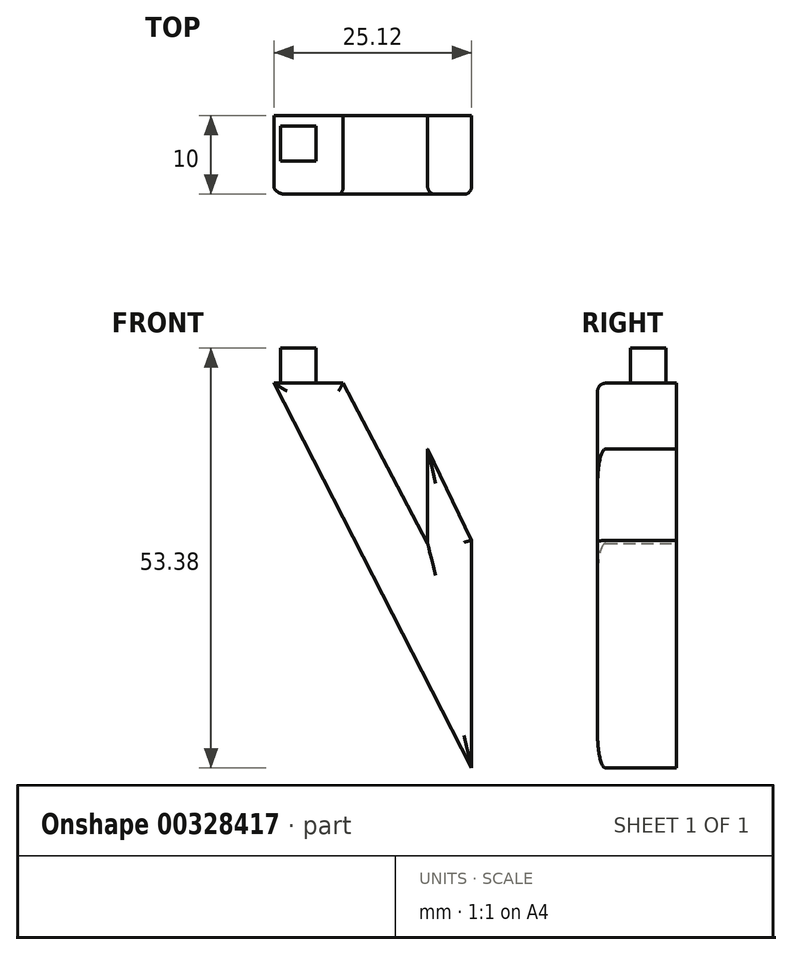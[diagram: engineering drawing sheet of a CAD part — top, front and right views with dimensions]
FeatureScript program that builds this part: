
annotation { "Feature Type Name" : "Feature", "Feature Type Description" : "" }
export const myFeature = defineFeature(function(context is Context, id is Id, definition is map)
    precondition{}
    {
        {
            var Q0;
            Q0=qCreatedBy(makeId("Front.planeOp"),FACE);
            var sketch = newSketch(context, id + "F0", { "sketchPlane" : qUnion([Q0])});
            skLineSegment(sketch, "E0", {"start": v(0, 0) * mm, "end": v(-9, 0) * mm});
            skLineSegment(sketch, "E1", {"start": v(0, 0) * mm, "end": v(10.72, -20.35) * mm});
            skLineSegment(sketch, "E2", {"start": v(10.72, -20.35) * mm, "end": v(10.72, -8.35) * mm});
            skLineSegment(sketch, "E3", {"start": v(10.72, -8.35) * mm, "end": v(16.31, -19.98) * mm});
            skLineSegment(sketch, "E4", {"start": v(16.31, -19.98) * mm, "end": v(16.31, -48.88) * mm});
            skLineSegment(sketch, "E5", {"start": v(16.31, -48.88) * mm, "end": v(-8.83, 0.04) * mm});
            skSolve(sketch);
        }
        {
            var Q0;
            {var subQ0=sQuery(id+"F0.wireOp",EDGE,"E1");Q0=makeQuery(id+"F0.imprint","IMPRINT",FACE,{"disambiguationData":[TD([[makeQuery(id+"F0.imprint","IMPRINT",EDGE,{"derivedFrom":subQ0}),-1.0]])]});}
            extrude(context, id + "F1", {"entities" : qUnion([Q0]), "depth" : 10 * mm});
        }
        {
            var Q0;
            Q0=makeQuery(id+"F1.opExtrude","CAP_EDGE",EDGE,{"disambiguationData":[OSD([sQuery(id+"F0.wireOp",EDGE,"E3")])],"isStart":false});
            var Q1;
            Q1=makeQuery(id+"F1.opExtrude","CAP_EDGE",EDGE,{"disambiguationData":[OSD([sQuery(id+"F0.wireOp",EDGE,"E5")])],"isStart":false});
            var Q2;
            Q2=makeQuery(id+"F1.opExtrude","CAP_EDGE",EDGE,{"disambiguationData":[OSD([sQuery(id+"F0.wireOp",EDGE,"E1")])],"isStart":false});
            var Q3;
            Q3=makeQuery(id+"F1.opExtrude","CAP_EDGE",EDGE,{"disambiguationData":[OSD([sQuery(id+"F0.wireOp",EDGE,"E2")])],"isStart":false});
            var Q4;
            Q4=makeQuery(id+"F1.opExtrude","CAP_EDGE",EDGE,{"disambiguationData":[OSD([sQuery(id+"F0.wireOp",EDGE,"E4")])],"isStart":false});
            var Q5;
            Q5=makeQuery(id+"F1.opExtrude","CAP_EDGE",EDGE,{"disambiguationData":[OSD([sQuery(id+"F0.wireOp",EDGE,"E0")])],"isStart":false});
            fillet(context, id + "F2", {"entities" : qUnion([Q0, Q1, Q2, Q3, Q4, Q5]), "radius" : 1 * mm, "tangentPropagation" : true, "allowEdgeOverflow" : false});
        }
        {
            var Q0;
            Q0=makeQuery(id+"F1.opExtrude","SWEPT_FACE",FACE,{"disambiguationData":[OSD([sQuery(id+"F0.wireOp",EDGE,"E0")])]});
            var sketch = newSketch(context, id + "F3", { "sketchPlane" : qUnion([Q0])});
            skLineSegment(sketch, "E6", {"start": v(-7.97, -5.81) * mm, "end": v(-7.97, -1.31) * mm});
            skLineSegment(sketch, "E7", {"start": v(-7.97, -1.31) * mm, "end": v(-3.47, -1.31) * mm});
            skLineSegment(sketch, "E8", {"start": v(-7.97, -5.81) * mm, "end": v(-3.47, -5.81) * mm});
            skLineSegment(sketch, "E9", {"start": v(-3.47, -1.31) * mm, "end": v(-3.47, -5.81) * mm});
            skSolve(sketch);
        }
        {
            var Q0;
            Q0=makeQuery(id+"F3.imprint","IMPRINT",FACE,{"disambiguationData":[TD([[makeQuery(id+"F3.imprint","IMPRINT",EDGE,{"derivedFrom":sQuery(id+"F3.wireOp",EDGE,"E6")}),-1.0]])]});
            extrude(context, id + "F4", {"entities" : qUnion([Q0]), "operationType" : NewBodyOperationType.ADD, "depth" : 4.5 * mm});
        }
    });
